# Revit family: QF_Southern Pride_SC-300
name_source: partatom
category: Specialty Equipment
units: mm (PartAtom-declared; Revit-internal decimal feet)

## family parameters
Always vertical = Yes
Cut with Voids When Loaded = No
OmniClass Number = 23.40.40.14.17.27
OmniClass Title = Barbecues
Part Type = Normal
Room Calculation Point = No
Round Connector Dimension = Use Diameter
Shared = No
Work Plane-Based = No

## types (1)
- QF_Southern Pride_SC-300
    Apparent Power = 6240 VA
    Assembly Code = E1090320
    CSI MasterFormat = 11 44 00
    Conn Conduit = Yes
    Cycle = 60 Hz
    Description = Stationary Rack Smoker, Electric Woodchip-Burning
    Elec Conn Connection Height = 13.375 "
    Electric Connection Type = 2 Wire (plus Ground)
    FL Amps = 30 A
    Foodservice Equipment Identifier = Yes
    Manufacturer = Southern Pride
    Model = SC-300
    Phase = 1
    URL = www.southernpride.com
    URL Cutsheet = https://www.southernpride.com
    Volts = 208 V
    Weight in Pounds = 300

## geometry (parser evidence)
native form markers: Sweep x10
no freeform markers — native parametric forms only
